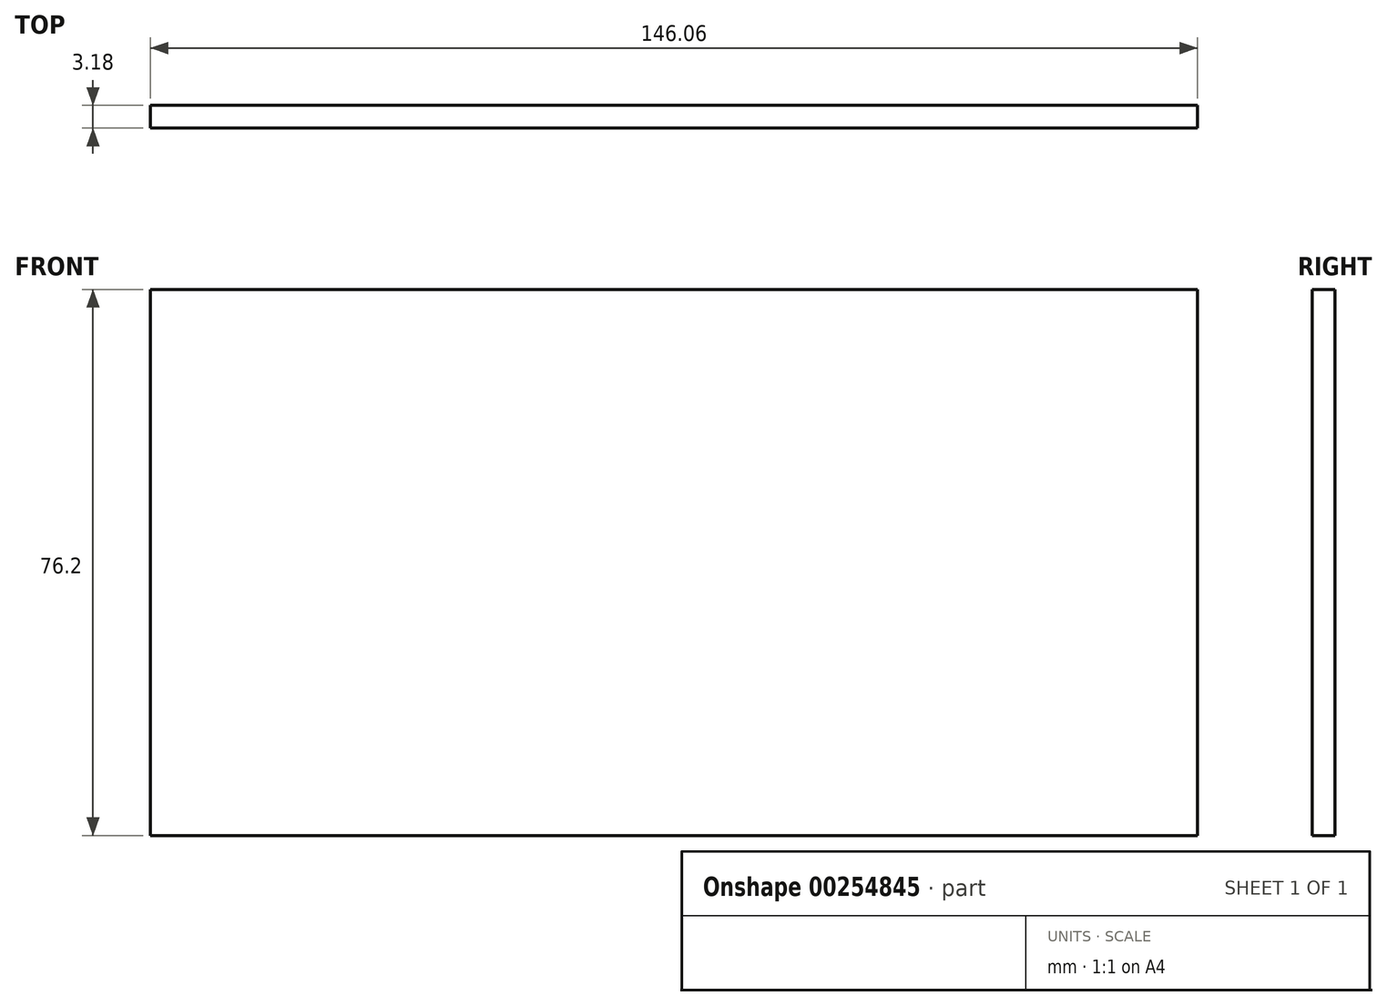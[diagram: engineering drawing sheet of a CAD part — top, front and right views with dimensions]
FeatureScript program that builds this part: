
annotation { "Feature Type Name" : "Feature", "Feature Type Description" : "" }
export const myFeature = defineFeature(function(context is Context, id is Id, definition is map)
    precondition{}
    {
        {
            var Q0;
            Q0=qCreatedBy(makeId("Front.planeOp"),FACE);
            var sketch = newSketch(context, id + "F0", { "sketchPlane" : qUnion([Q0])});
            skLineSegment(sketch, "E0.bottom", {"start": v(-73.03, -38.1) * mm, "end": v(73.03, -38.1) * mm});
            skLineSegment(sketch, "E0.top", {"start": v(-73.03, 38.1) * mm, "end": v(73.03, 38.1) * mm});
            skLineSegment(sketch, "E0.left", {"start": v(-73.03, -38.1) * mm, "end": v(-73.03, 38.1) * mm});
            skLineSegment(sketch, "E0.right", {"start": v(73.03, -38.1) * mm, "end": v(73.03, 38.1) * mm});
            skPoint(sketch, "E0.middle", {"position": v(0, 0) * mm});
            skSolve(sketch);
        }
        {
            var Q0;
            Q0=makeQuery(id+"F0.imprint","IMPRINT",FACE,{"disambiguationData":[TD([[makeQuery(id+"F0.imprint","IMPRINT",EDGE,{"derivedFrom":sQuery(id+"F0.wireOp",EDGE,"E0.bottom")}),1.0]])]});
            extrude(context, id + "F1", {"entities" : qUnion([Q0]), "endBound" : BoundingType.SYMMETRIC, "depth" : 3.17 * mm});
        }
    });
